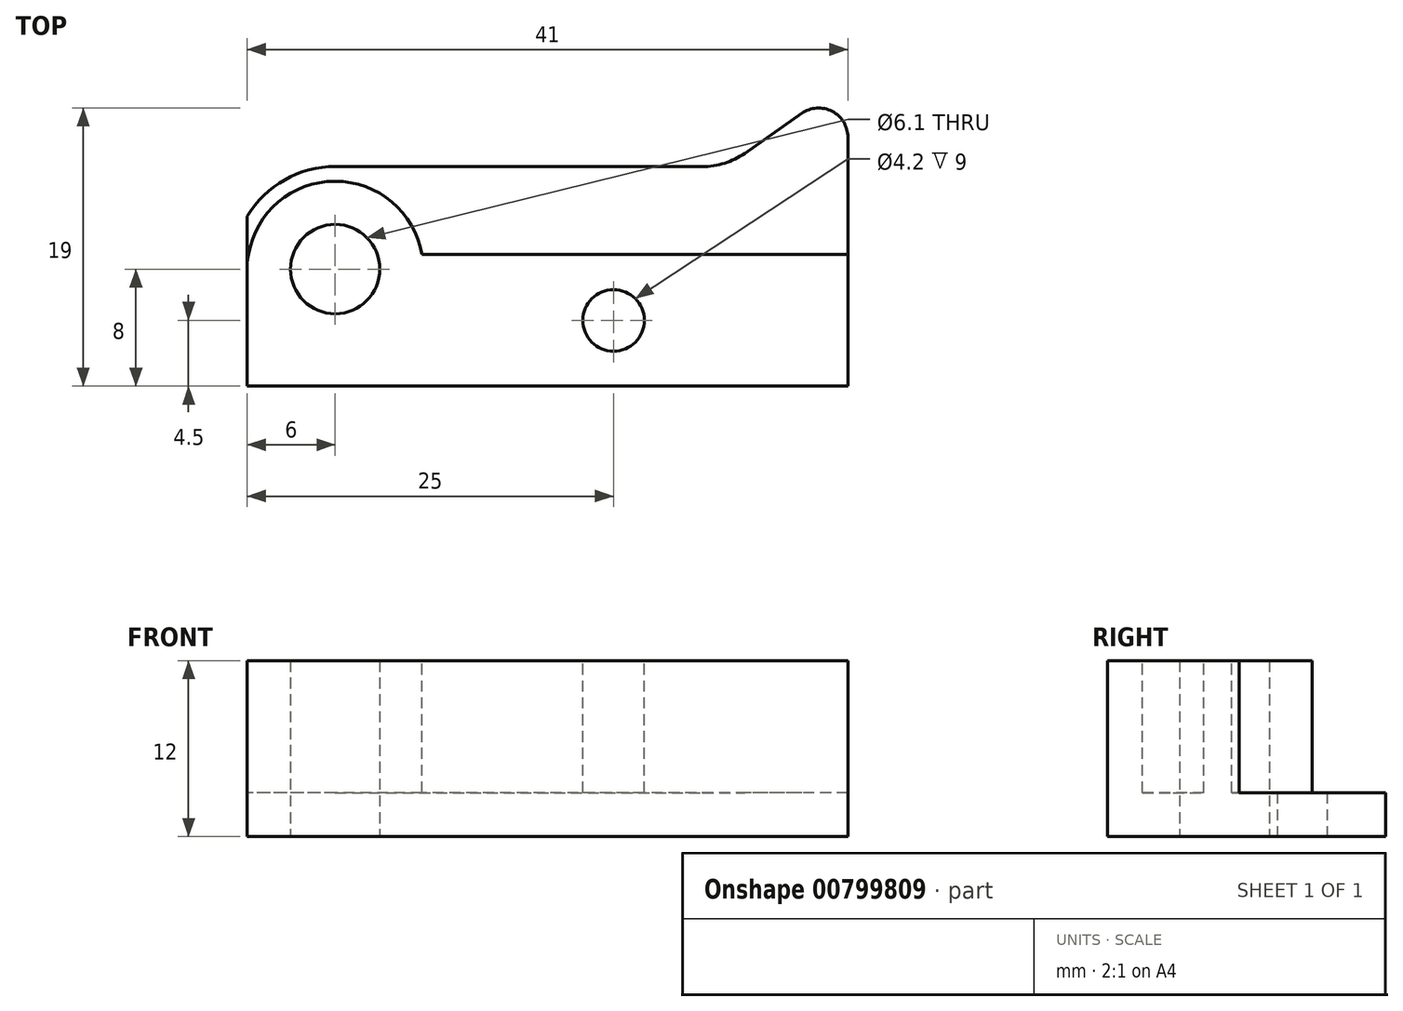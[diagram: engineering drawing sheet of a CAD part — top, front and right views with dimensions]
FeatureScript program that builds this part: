
annotation { "Feature Type Name" : "Feature", "Feature Type Description" : "" }
export const myFeature = defineFeature(function(context is Context, id is Id, definition is map)
    precondition{}
    {
        {
            var Q0;
            Q0=qCreatedBy(makeId("Top.planeOp"),FACE);
            var sketch = newSketch(context, id + "F0", { "sketchPlane" : qUnion([Q0])});
            skLineSegment(sketch, "E0", {"start": v(0, 0) * mm, "end": v(0, 11.6) * mm});
            skLineSegment(sketch, "E1", {"start": v(6, 15) * mm, "end": v(31.08, 15) * mm});
            skLineSegment(sketch, "E2", {"start": v(41, 15) * mm, "end": v(41, 0) * mm});
            skLineSegment(sketch, "E3", {"start": v(41, 0) * mm, "end": v(0, 0) * mm});
            skCircle(sketch, "E4", {"center": v(6, 8) * mm, "radius": 3.05 * mm});
            skArc(sketch, "E5", {"start": v(6, 15) * mm, "mid": v(2.55, 14.1) * mm, "end": v(0, 11.6) * mm});
            skLineSegment(sketch, "E6", {"start": v(41, 15) * mm, "end": v(41, 17) * mm});
            skLineSegment(sketch, "E7", {"start": v(37.85, 18.64) * mm, "end": v(33.95, 15.9) * mm});
            skPoint(sketch, "E8.visualSharp", {"position": v(32.66, 15) * mm});
            skArc(sketch, "E8.filletArc", {"start": v(31.08, 15) * mm, "mid": v(32.58, 15.23) * mm, "end": v(33.95, 15.9) * mm});
            skArc(sketch, "E9", {"start": v(41, 17) * mm, "mid": v(39.92, 18.77) * mm, "end": v(37.85, 18.64) * mm});
            skSolve(sketch);
        }
        {
            var Q0;
            Q0=makeQuery(id+"F0.imprint","IMPRINT",FACE,{"disambiguationData":[TD([[makeQuery(id+"F0.imprint","IMPRINT",EDGE,{"derivedFrom":sQuery(id+"F0.wireOp",EDGE,"E0")}),-1.0]])]});
            extrude(context, id + "F1", {"entities" : qUnion([Q0]), "depth" : 12 * mm, "offsetDistance" : 25 * mm});
        }
        {
            var Q0;
            Q0=makeQuery(id+"F1.opExtrude","CAP_FACE",FACE,{"disambiguationData":[OSD([sQuery(id+"F0.wireOp",EDGE,"E0"),sQuery(id+"F0.wireOp",EDGE,"E1"),sQuery(id+"F0.wireOp",EDGE,"E2"),sQuery(id+"F0.wireOp",EDGE,"E3"),sQuery(id+"F0.wireOp",EDGE,"E4"),sQuery(id+"F0.wireOp",EDGE,"E5"),sQuery(id+"F0.wireOp",EDGE,"E6"),sQuery(id+"F0.wireOp",EDGE,"E7"),sQuery(id+"F0.wireOp",EDGE,"E8.filletArc"),sQuery(id+"F0.wireOp",EDGE,"E9")])],"isStart":false});
            var sketch = newSketch(context, id + "F2", { "sketchPlane" : qUnion([Q0])});
            skLineSegment(sketch, "E10", {"start": v(41, 9) * mm, "end": v(11.92, 9) * mm});
            skArc(sketch, "E11", {"start": v(11.92, 9) * mm, "mid": v(6, 14) * mm, "end": v(0.08, 9) * mm});
            skLineSegment(sketch, "E12", {"start": v(0.08, 9) * mm, "end": v(0, 8.5) * mm});
            skLineSegment(sketch, "E13.0", {"start": v(0, 8.5) * mm, "end": v(0, 11.6) * mm});
            skArc(sketch, "E14.0", {"start": v(6, 15) * mm, "mid": v(2.55, 14.1) * mm, "end": v(0, 11.6) * mm});
            skLineSegment(sketch, "E15.0", {"start": v(6, 15) * mm, "end": v(31.08, 15) * mm});
            skArc(sketch, "E16.0", {"start": v(31.08, 15) * mm, "mid": v(32.58, 15.23) * mm, "end": v(33.95, 15.9) * mm});
            skLineSegment(sketch, "E17.0", {"start": v(37.85, 18.64) * mm, "end": v(33.95, 15.9) * mm});
            skArc(sketch, "E18.0", {"start": v(41, 17) * mm, "mid": v(39.92, 18.77) * mm, "end": v(37.85, 18.64) * mm});
            skLineSegment(sketch, "E19.0", {"start": v(41, 17) * mm, "end": v(41, 9) * mm});
            skPoint(sketch, "E20.orphan", {"position": v(41, 0) * mm});
            skPoint(sketch, "E21.orphan", {"position": v(0, 0) * mm});
            skCircle(sketch, "E22", {"center": v(25, 4.5) * mm, "radius": 2.1 * mm});
            skSolve(sketch);
        }
        {
            var Q0;
            Q0=makeQuery(id+"F2.imprint","IMPRINT",FACE,{"disambiguationData":[TD([[makeQuery(id+"F2.imprint","IMPRINT",EDGE,{"derivedFrom":sQuery(id+"F2.wireOp",EDGE,"E10")}),-1.0]])]});
            var Q1;
            Q1=makeQuery(id+"F2.imprint","IMPRINT",FACE,{"disambiguationData":[TD([[makeQuery(id+"F2.imprint","IMPRINT",EDGE,{"derivedFrom":sQuery(id+"F2.wireOp",EDGE,"E22")}),1.0]])]});
            extrude(context, id + "F3", {"entities" : qUnion([Q0, Q1]), "operationType" : NewBodyOperationType.REMOVE, "oppositeDirection" : true, "depth" : 9 * mm, "offsetDistance" : 25 * mm});
        }
    });
